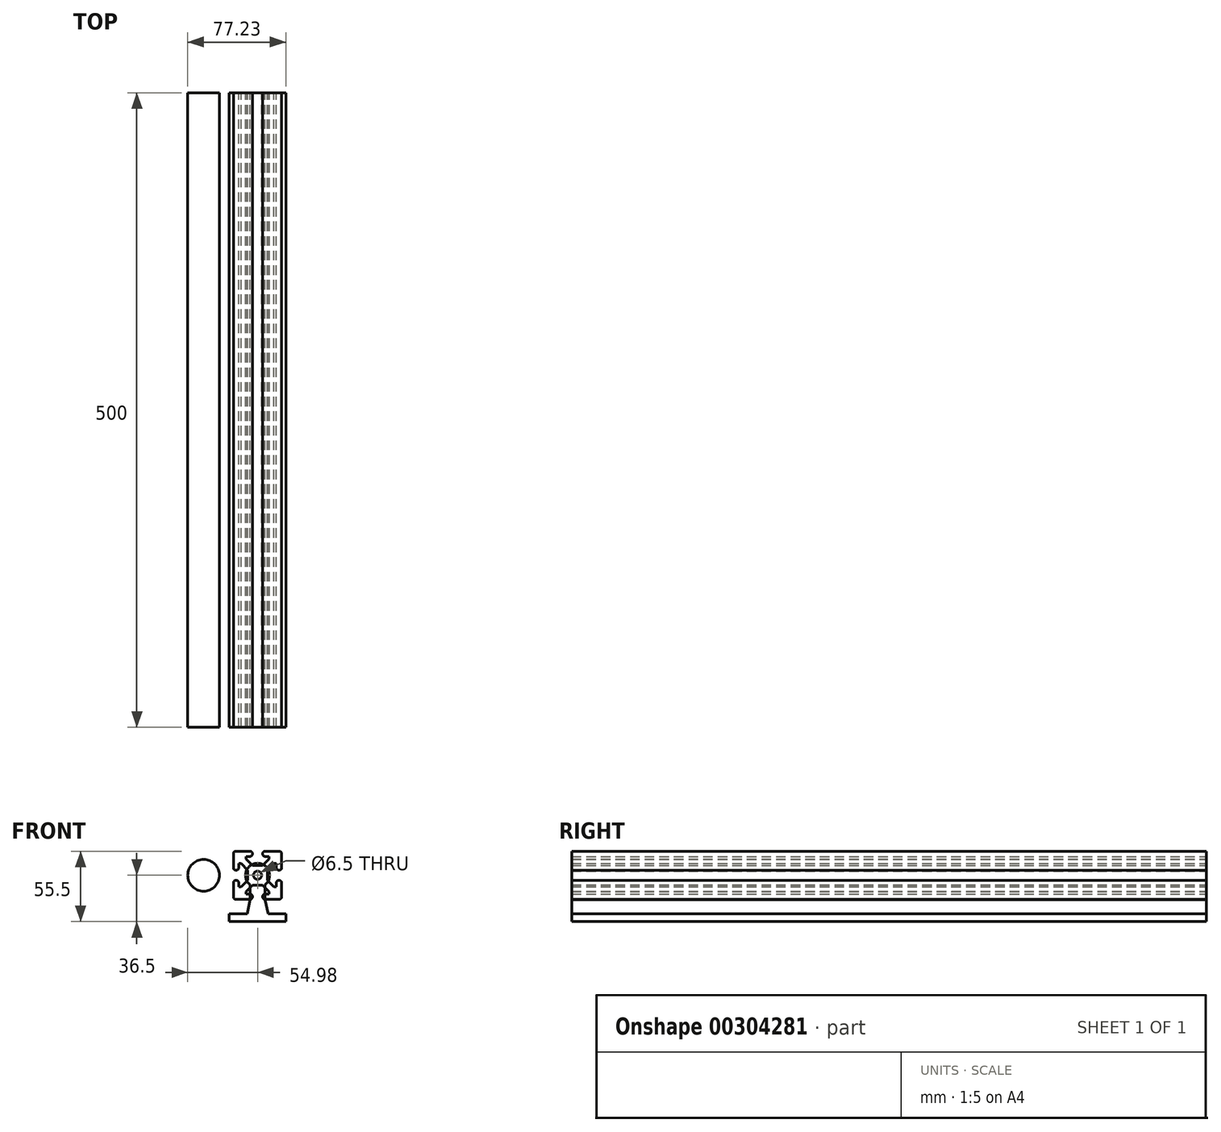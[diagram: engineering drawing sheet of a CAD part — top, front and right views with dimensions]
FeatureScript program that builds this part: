
annotation { "Feature Type Name" : "Feature", "Feature Type Description" : "" }
export const myFeature = defineFeature(function(context is Context, id is Id, definition is map)
    precondition{}
    {
        {
            var Q0;
            Q0=qCreatedBy(makeId("Front.planeOp"),FACE);
            var sketch = newSketch(context, id + "F0", { "sketchPlane" : qUnion([Q0])});
            skCircle(sketch, "E0", {"center": v(0, 0) * mm, "radius": 9.5 * mm});
            skLineSegment(sketch, "E1", {"start": v(0, 9.5) * mm, "end": v(0, -36.5) * mm, "construction": true});
            skLineSegment(sketch, "E2", {"start": v(-22.25, -36.5) * mm, "end": v(22.25, -36.5) * mm});
            skLineSegment(sketch, "E3", {"start": v(-22.25, -36.5) * mm, "end": v(-22.25, -30.5) * mm});
            skLineSegment(sketch, "E4", {"start": v(22.25, -30.5) * mm, "end": v(22.25, -36.5) * mm});
            skLineSegment(sketch, "E5", {"start": v(-6, -7.37) * mm, "end": v(6, -7.37) * mm});
            skLineSegment(sketch, "E6", {"start": v(-6, -7.37) * mm, "end": v(-6, -19.37) * mm});
            skLineSegment(sketch, "E7", {"start": v(-6, -19.37) * mm, "end": v(6, -19.37) * mm});
            skLineSegment(sketch, "E8", {"start": v(6, -19.37) * mm, "end": v(6, -7.37) * mm});
            skLineSegment(sketch, "E9", {"start": v(-22.25, -30.5) * mm, "end": v(-8.25, -30.5) * mm});
            skLineSegment(sketch, "E10", {"start": v(-8.25, -30.5) * mm, "end": v(8.25, -30.5) * mm});
            skLineSegment(sketch, "E11", {"start": v(8.25, -30.5) * mm, "end": v(22.25, -30.5) * mm});
            skLineSegment(sketch, "E12", {"start": v(-6, -19.37) * mm, "end": v(-8.25, -30.5) * mm});
            skLineSegment(sketch, "E13", {"start": v(6, -19.37) * mm, "end": v(8.25, -30.5) * mm});
            skSolve(sketch);
        }
        {
            var Q0;
            Q0 = qSketchRegion(id + "F0", true);
            extrude(context, id + "F1", {"entities" : qUnion([Q0]), "depth" : 500 * mm});
        }
        {
            var Q0;
            Q0=qCreatedBy(makeId("Front.planeOp"),FACE);
            var sketch = newSketch(context, id + "F2", { "sketchPlane" : qUnion([Q0])});
            skCircle(sketch, "E14", {"center": v(-42.48, 0) * mm, "radius": 12.5 * mm});
            skSolve(sketch);
        }
        {
            var Q0;
            Q0 = qSketchRegion(id + "F2", true);
            extrude(context, id + "F3", {"entities" : qUnion([Q0]), "depth" : 500 * mm});
        }
        {
            var Q0;
            Q0=qCreatedBy(makeId("Front.planeOp"),FACE);
            var sketch = newSketch(context, id + "F4", { "sketchPlane" : qUnion([Q0])});
            skCircle(sketch, "E15", {"center": v(0, 0) * mm, "radius": 3.25 * mm});
            skLineSegment(sketch, "E16", {"start": v(0, 19) * mm, "end": v(0, -19) * mm, "construction": true});
            skLineSegment(sketch, "E17", {"start": v(-19, 0) * mm, "end": v(19, 0) * mm, "construction": true});
            skLineSegment(sketch, "E18", {"start": v(-4, 19) * mm, "end": v(4, 19) * mm, "construction": true});
            skLineSegment(sketch, "E19", {"start": v(-19, 4) * mm, "end": v(-19, -4) * mm, "construction": true});
            skLineSegment(sketch, "E20", {"start": v(19, 4) * mm, "end": v(19, -4) * mm, "construction": true});
            skLineSegment(sketch, "E21", {"start": v(-4, -19) * mm, "end": v(4, -19) * mm, "construction": true});
            skLineSegment(sketch, "E22", {"start": v(4, 19) * mm, "end": v(19, 19) * mm});
            skLineSegment(sketch, "E23", {"start": v(19, 19) * mm, "end": v(19, 4) * mm});
            skLineSegment(sketch, "E24", {"start": v(19, -4) * mm, "end": v(19, -19) * mm});
            skLineSegment(sketch, "E25", {"start": v(19, -19) * mm, "end": v(4, -19) * mm});
            skLineSegment(sketch, "E26", {"start": v(-4, -19) * mm, "end": v(-19, -19) * mm});
            skLineSegment(sketch, "E27", {"start": v(-19, -19) * mm, "end": v(-19, -4) * mm});
            skLineSegment(sketch, "E28", {"start": v(-19, 4) * mm, "end": v(-19, 19) * mm});
            skLineSegment(sketch, "E29", {"start": v(-19, 19) * mm, "end": v(-4, 19) * mm});
            skLineSegment(sketch, "E30", {"start": v(4, 19) * mm, "end": v(4, 14.8) * mm});
            skLineSegment(sketch, "E31", {"start": v(4, 14.8) * mm, "end": v(9.2, 14.8) * mm});
            skLineSegment(sketch, "E32", {"start": v(-4, 19) * mm, "end": v(-4, 14.8) * mm});
            skLineSegment(sketch, "E33", {"start": v(-4, 14.8) * mm, "end": v(-9.2, 14.8) * mm});
            skLineSegment(sketch, "E34", {"start": v(-19, 4) * mm, "end": v(-14.8, 4) * mm});
            skLineSegment(sketch, "E35", {"start": v(-14.8, 4) * mm, "end": v(-14.8, 9.2) * mm});
            skLineSegment(sketch, "E36", {"start": v(-19, -4) * mm, "end": v(-14.8, -4) * mm});
            skLineSegment(sketch, "E37", {"start": v(-14.8, -4) * mm, "end": v(-14.8, -9.2) * mm});
            skLineSegment(sketch, "E38", {"start": v(-4, -19) * mm, "end": v(-4, -14.8) * mm});
            skLineSegment(sketch, "E39", {"start": v(-4, -14.8) * mm, "end": v(-9.2, -14.8) * mm});
            skLineSegment(sketch, "E40", {"start": v(4, -19) * mm, "end": v(4, -14.8) * mm});
            skLineSegment(sketch, "E41", {"start": v(4, -14.8) * mm, "end": v(9.2, -14.8) * mm});
            skLineSegment(sketch, "E42", {"start": v(19, -4) * mm, "end": v(14.8, -4) * mm});
            skLineSegment(sketch, "E43", {"start": v(14.8, -4) * mm, "end": v(14.8, -9.2) * mm});
            skLineSegment(sketch, "E44", {"start": v(19, 4) * mm, "end": v(14.8, 4) * mm});
            skLineSegment(sketch, "E45", {"start": v(14.8, 4) * mm, "end": v(14.8, 9.2) * mm});
            skLineSegment(sketch, "E46", {"start": v(-9.2, 14.8) * mm, "end": v(-9.2, 12.8) * mm});
            skLineSegment(sketch, "E47", {"start": v(-14.8, 9.2) * mm, "end": v(-12.8, 9.2) * mm});
            skLineSegment(sketch, "E48", {"start": v(9.2, 14.8) * mm, "end": v(9.2, 12.8) * mm});
            skLineSegment(sketch, "E49", {"start": v(14.8, 9.2) * mm, "end": v(12.8, 9.2) * mm});
            skLineSegment(sketch, "E50", {"start": v(14.8, -9.2) * mm, "end": v(12.8, -9.2) * mm});
            skLineSegment(sketch, "E51", {"start": v(9.2, -14.8) * mm, "end": v(9.2, -12.8) * mm});
            skLineSegment(sketch, "E52", {"start": v(-9.2, -14.8) * mm, "end": v(-9.2, -12.8) * mm});
            skLineSegment(sketch, "E53", {"start": v(-14.8, -9.2) * mm, "end": v(-12.8, -9.2) * mm});
            skLineSegment(sketch, "E54", {"start": v(-7.9, 0) * mm, "end": v(7.9, 0) * mm, "construction": true});
            skLineSegment(sketch, "E55", {"start": v(0, 7.9) * mm, "end": v(0, -7.9) * mm, "construction": true});
            skLineSegment(sketch, "E56", {"start": v(-4, 7.9) * mm, "end": v(4, 7.9) * mm});
            skLineSegment(sketch, "E57", {"start": v(-4, -7.9) * mm, "end": v(4, -7.9) * mm});
            skLineSegment(sketch, "E58", {"start": v(7.9, 4) * mm, "end": v(7.9, -4) * mm});
            skLineSegment(sketch, "E59", {"start": v(-7.9, 4) * mm, "end": v(-7.9, -4) * mm});
            skLineSegment(sketch, "E60", {"start": v(-12.8, 9.2) * mm, "end": v(-7.9, 4) * mm});
            skLineSegment(sketch, "E61", {"start": v(-9.2, 12.8) * mm, "end": v(-4, 7.9) * mm});
            skLineSegment(sketch, "E62", {"start": v(4, 7.9) * mm, "end": v(9.2, 12.8) * mm});
            skLineSegment(sketch, "E63", {"start": v(7.9, 4) * mm, "end": v(12.8, 9.2) * mm});
            skLineSegment(sketch, "E64", {"start": v(7.9, -4) * mm, "end": v(12.8, -9.2) * mm});
            skLineSegment(sketch, "E65", {"start": v(9.2, -12.8) * mm, "end": v(4, -7.9) * mm});
            skLineSegment(sketch, "E66", {"start": v(-4, -7.9) * mm, "end": v(-9.2, -12.8) * mm});
            skLineSegment(sketch, "E67", {"start": v(-12.8, -9.2) * mm, "end": v(-7.9, -4) * mm});
            skSolve(sketch);
        }
        {
            var Q0;
            Q0 = qSketchRegion(id + "F4", true);
            extrude(context, id + "F5", {"entities" : qUnion([Q0]), "depth" : 500 * mm});
        }
        {
            var Q0;
            Q0=makeQuery(id+"F5.opExtrude","SWEPT_EDGE",EDGE,{"disambiguationData":[OSD([sQuery(id+"F4.wireOp",EDGE,"E28"),sQuery(id+"F4.wireOp",EDGE,"E29")])]});
            var Q1;
            Q1=makeQuery(id+"F5.opExtrude","SWEPT_EDGE",EDGE,{"disambiguationData":[OSD([sQuery(id+"F4.wireOp",EDGE,"E22"),sQuery(id+"F4.wireOp",EDGE,"E23")])]});
            var Q2;
            Q2=makeQuery(id+"F5.opExtrude","SWEPT_EDGE",EDGE,{"disambiguationData":[OSD([sQuery(id+"F4.wireOp",EDGE,"E23"),sQuery(id+"F4.wireOp",EDGE,"E44")])]});
            var Q3;
            Q3=makeQuery(id+"F5.opExtrude","SWEPT_EDGE",EDGE,{"disambiguationData":[OSD([sQuery(id+"F4.wireOp",EDGE,"E24"),sQuery(id+"F4.wireOp",EDGE,"E42")])]});
            var Q4;
            Q4=makeQuery(id+"F5.opExtrude","SWEPT_EDGE",EDGE,{"disambiguationData":[OSD([sQuery(id+"F4.wireOp",EDGE,"E24"),sQuery(id+"F4.wireOp",EDGE,"E25")])]});
            var Q5;
            Q5=makeQuery(id+"F5.opExtrude","SWEPT_EDGE",EDGE,{"disambiguationData":[OSD([sQuery(id+"F4.wireOp",EDGE,"E26"),sQuery(id+"F4.wireOp",EDGE,"E38")])]});
            var Q6;
            Q6=makeQuery(id+"F5.opExtrude","SWEPT_EDGE",EDGE,{"disambiguationData":[OSD([sQuery(id+"F4.wireOp",EDGE,"E29"),sQuery(id+"F4.wireOp",EDGE,"E32")])]});
            var Q7;
            Q7=makeQuery(id+"F5.opExtrude","SWEPT_EDGE",EDGE,{"disambiguationData":[OSD([sQuery(id+"F4.wireOp",EDGE,"E22"),sQuery(id+"F4.wireOp",EDGE,"E30")])]});
            var Q8;
            Q8=makeQuery(id+"F5.opExtrude","SWEPT_EDGE",EDGE,{"disambiguationData":[OSD([sQuery(id+"F4.wireOp",EDGE,"E34"),sQuery(id+"F4.wireOp",EDGE,"E35")])]});
            var Q9;
            Q9=makeQuery(id+"F5.opExtrude","SWEPT_EDGE",EDGE,{"disambiguationData":[OSD([sQuery(id+"F4.wireOp",EDGE,"E27"),sQuery(id+"F4.wireOp",EDGE,"E36")])]});
            var Q10;
            Q10=makeQuery(id+"F5.opExtrude","SWEPT_EDGE",EDGE,{"disambiguationData":[OSD([sQuery(id+"F4.wireOp",EDGE,"E26"),sQuery(id+"F4.wireOp",EDGE,"E27")])]});
            var Q11;
            Q11=makeQuery(id+"F5.opExtrude","SWEPT_EDGE",EDGE,{"disambiguationData":[OSD([sQuery(id+"F4.wireOp",EDGE,"E25"),sQuery(id+"F4.wireOp",EDGE,"E40")])]});
            var Q12;
            Q12=makeQuery(id+"F5.opExtrude","SWEPT_EDGE",EDGE,{"disambiguationData":[OSD([sQuery(id+"F4.wireOp",EDGE,"E40"),sQuery(id+"F4.wireOp",EDGE,"E41")])]});
            var Q13;
            Q13=makeQuery(id+"F5.opExtrude","SWEPT_EDGE",EDGE,{"disambiguationData":[OSD([sQuery(id+"F4.wireOp",EDGE,"E42"),sQuery(id+"F4.wireOp",EDGE,"E43")])]});
            var Q14;
            Q14=makeQuery(id+"F5.opExtrude","SWEPT_EDGE",EDGE,{"disambiguationData":[OSD([sQuery(id+"F4.wireOp",EDGE,"E44"),sQuery(id+"F4.wireOp",EDGE,"E45")])]});
            var Q15;
            Q15=makeQuery(id+"F5.opExtrude","SWEPT_EDGE",EDGE,{"disambiguationData":[OSD([sQuery(id+"F4.wireOp",EDGE,"E30"),sQuery(id+"F4.wireOp",EDGE,"E31")])]});
            var Q16;
            Q16=makeQuery(id+"F5.opExtrude","SWEPT_EDGE",EDGE,{"disambiguationData":[OSD([sQuery(id+"F4.wireOp",EDGE,"E28"),sQuery(id+"F4.wireOp",EDGE,"E34")])]});
            var Q17;
            Q17=makeQuery(id+"F5.opExtrude","SWEPT_EDGE",EDGE,{"disambiguationData":[OSD([sQuery(id+"F4.wireOp",EDGE,"E36"),sQuery(id+"F4.wireOp",EDGE,"E37")])]});
            var Q18;
            Q18=makeQuery(id+"F5.opExtrude","SWEPT_EDGE",EDGE,{"disambiguationData":[OSD([sQuery(id+"F4.wireOp",EDGE,"E38"),sQuery(id+"F4.wireOp",EDGE,"E39")])]});
            var Q19;
            Q19=makeQuery(id+"F5.opExtrude","SWEPT_EDGE",EDGE,{"disambiguationData":[OSD([sQuery(id+"F4.wireOp",EDGE,"E32"),sQuery(id+"F4.wireOp",EDGE,"E33")])]});
            fillet(context, id + "F6", {"entities" : qUnion([Q0, Q1, Q2, Q3, Q4, Q5, Q6, Q7, Q8, Q9, Q10, Q11, Q12, Q13, Q14, Q15, Q16, Q17, Q18, Q19]), "radius" : 2 * mm, "tangentPropagation" : true, "allowEdgeOverflow" : false});
        }
    });
